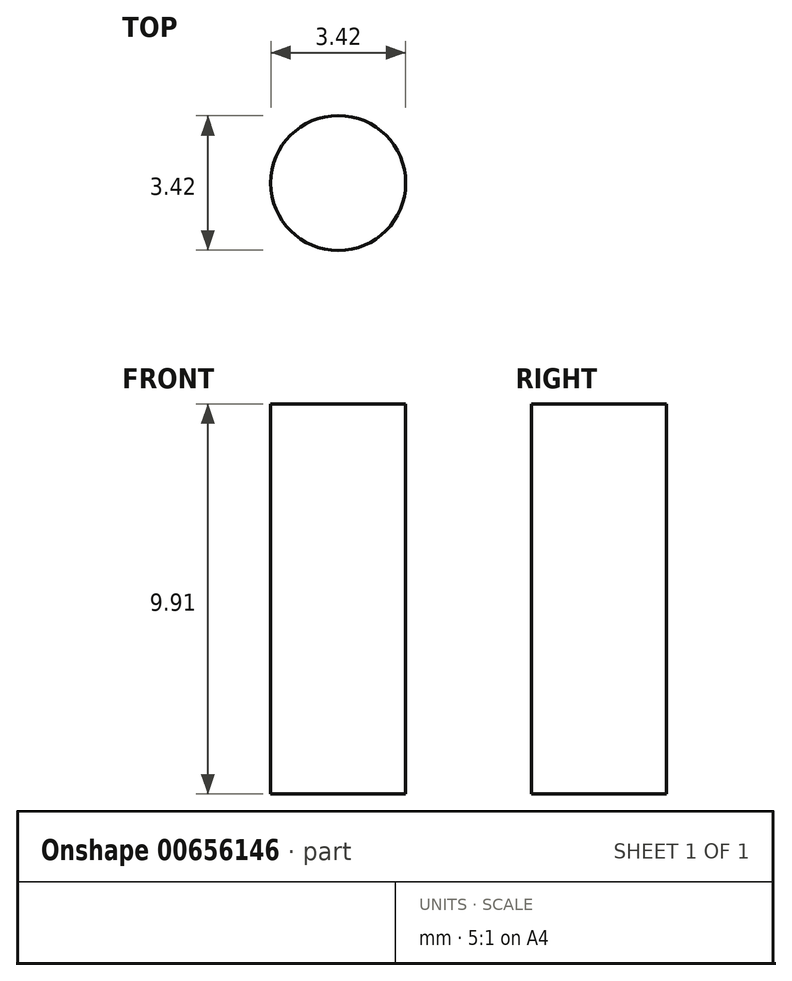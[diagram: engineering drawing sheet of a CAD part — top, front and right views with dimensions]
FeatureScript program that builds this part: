
annotation { "Feature Type Name" : "Feature", "Feature Type Description" : "" }
export const myFeature = defineFeature(function(context is Context, id is Id, definition is map)
    precondition{}
    {
        {
            var Q0;
            Q0=qCreatedBy(makeId("Top.planeOp"),FACE);
            var sketch = newSketch(context, id + "F0", { "sketchPlane" : qUnion([Q0])});
            skCircle(sketch, "E0", {"center": v(0, 0) * mm, "radius": 1.71 * mm});
            skSolve(sketch);
        }
        {
            var Q0;
            Q0 = qSketchRegion(id + "F0", true);
            extrude(context, id + "F1", {"entities" : qUnion([Q0]), "depth" : 9.9 * mm, "offsetDistance" : 25.4 * mm});
        }
    });
